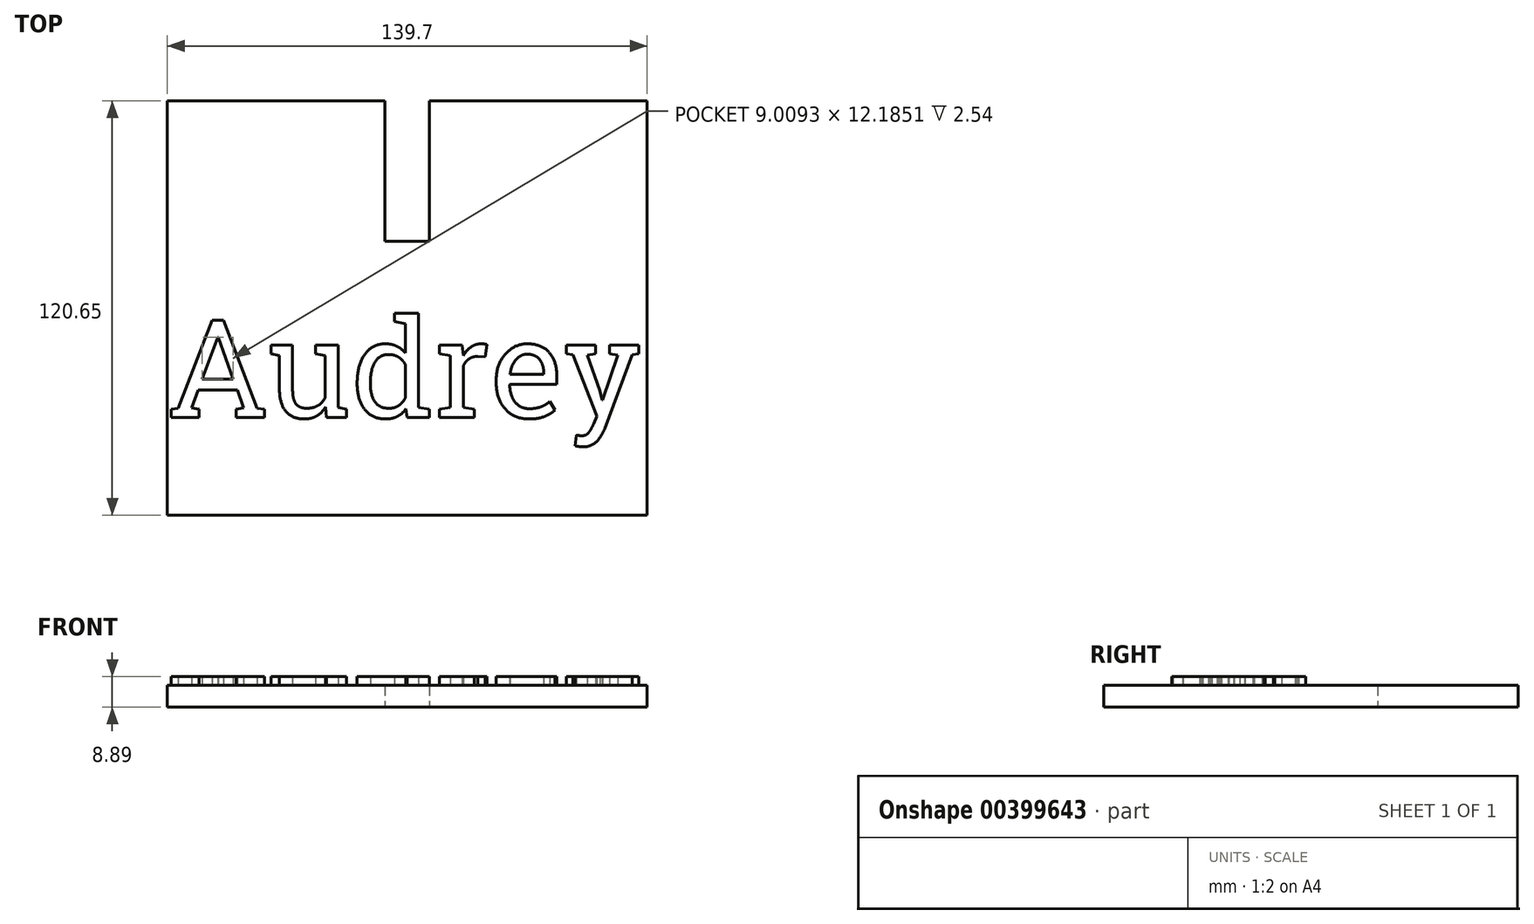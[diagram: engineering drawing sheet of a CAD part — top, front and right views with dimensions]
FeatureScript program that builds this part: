
annotation { "Feature Type Name" : "Feature", "Feature Type Description" : "" }
export const myFeature = defineFeature(function(context is Context, id is Id, definition is map)
    precondition{}
    {
        {
            var Q0;
            Q0=qCreatedBy(makeId("Top.planeOp"),FACE);
            var sketch = newSketch(context, id + "F0", { "sketchPlane" : qUnion([Q0])});
            skLineSegment(sketch, "E0.bottom", {"start": v(-69.85, 63.5) * mm, "end": v(69.85, 63.5) * mm});
            skLineSegment(sketch, "E0.top", {"start": v(-69.85, -57.15) * mm, "end": v(69.85, -57.15) * mm});
            skLineSegment(sketch, "E0.left", {"start": v(-69.85, 63.5) * mm, "end": v(-69.85, -57.15) * mm});
            skLineSegment(sketch, "E0.right", {"start": v(69.85, 63.5) * mm, "end": v(69.85, -57.15) * mm});
            skLineSegment(sketch, "E1.bottom", {"start": v(-6.48, 63.5) * mm, "end": v(6.48, 63.5) * mm});
            skLineSegment(sketch, "E1.top", {"start": v(-6.48, 22.6) * mm, "end": v(6.48, 22.6) * mm});
            skLineSegment(sketch, "E1.left", {"start": v(-6.48, 63.5) * mm, "end": v(-6.48, 22.6) * mm});
            skLineSegment(sketch, "E1.right", {"start": v(6.48, 63.5) * mm, "end": v(6.48, 22.6) * mm});
            skSolve(sketch);
        }
        {
            var Q0;
            Q0=makeQuery(id+"F0.imprint","IMPRINT",FACE,{"disambiguationData":[TD([[makeQuery(id+"F0.imprint","IMPRINT",EDGE,{"derivedFrom":sQuery(id+"F0.wireOp",EDGE,"E0.top")}),1.0]])]});
            extrude(context, id + "F1", {"entities" : qUnion([Q0]), "endBound" : BoundingType.SYMMETRIC, "depth" : 6.35 * mm});
        }
        {
            var Q0;
            Q0=makeQuery(id+"F1.opExtrude","CAP_FACE",FACE,{"disambiguationData":[OSD([sQuery(id+"F0.wireOp",EDGE,"E0.bottom"),sQuery(id+"F0.wireOp",EDGE,"E0.top"),sQuery(id+"F0.wireOp",EDGE,"E0.left"),sQuery(id+"F0.wireOp",EDGE,"E0.right"),sQuery(id+"F0.wireOp",EDGE,"E1.top"),sQuery(id+"F0.wireOp",EDGE,"E1.left"),sQuery(id+"F0.wireOp",EDGE,"E1.right")])],"isStart":false});
            var sketch = newSketch(context, id + "F2", { "sketchPlane" : qUnion([Q0])});
            skText(sketch, "E2", { "text": "Audrey", "fontName": "RobotoSlab-Regular.ttf"});
            const initialGuessF2  = {"E2": [-0.06985, -0.02875, 1, 0, 0.02875]};
            skSetInitialGuess(sketch, initialGuessF2);
            skSolve(sketch);
        }
        {
            var Q0;
            Q0 = qSketchRegion(id + "F2", true);
            extrude(context, id + "F3", {"entities" : qUnion([Q0]), "operationType" : NewBodyOperationType.ADD, "depth" : 2.54 * mm});
        }
    });
